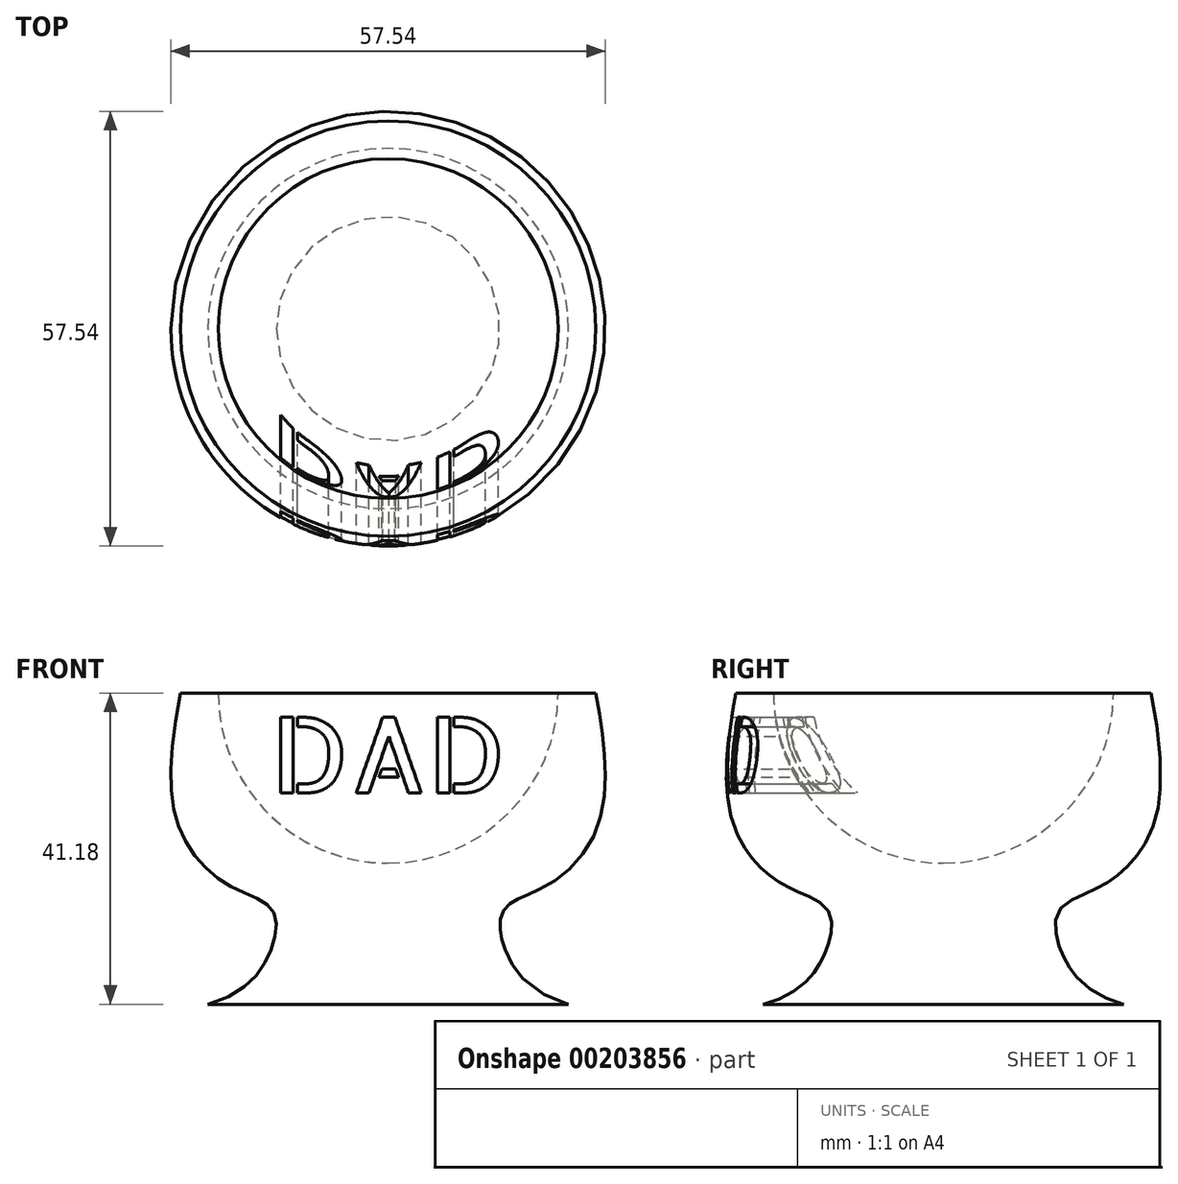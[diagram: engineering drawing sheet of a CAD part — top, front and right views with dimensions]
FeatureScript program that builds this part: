
annotation { "Feature Type Name" : "Feature", "Feature Type Description" : "" }
export const myFeature = defineFeature(function(context is Context, id is Id, definition is map)
    precondition{}
    {
        {
            var Q0;
            Q0=qCreatedBy(makeId("Front.planeOp"),FACE);
            var sketch = newSketch(context, id + "F0", { "sketchPlane" : qUnion([Q0])});
            skLineSegment(sketch, "E0", {"start": v(0, 0) * mm, "end": v(0, 41.18) * mm});
            skLineSegment(sketch, "E1", {"start": v(0, 0) * mm, "end": v(-23.86, 0) * mm});
            skCircle(sketch, "E2", {"center": v(0, 41.18) * mm, "radius": 22.5 * mm});
            skFitSpline(sketch, "E3", {"points": [v(-27.5, 41.18) * mm, v(-27.5, 22.94) * mm, v(-20.94, 15.67) * mm, v(-15.35, 12.49) * mm, v(-15.6, 6.98) * mm, v(-23.86, 0) * mm], "startDerivative": vector(-16.83, -89.57) * mm, "endDerivative": vector(-70.58, -19.3) * mm});
            skLineSegment(sketch, "E4", {"start": v(-22.5, 41.18) * mm, "end": v(-27.5, 41.18) * mm});
            skSolve(sketch);
        }
        {
            var Q0;
            {var subQ4=sQuery(id+"F0.wireOp",EDGE,"E1");Q0=makeQuery(id+"F0.imprint","IMPRINT",FACE,{"disambiguationData":[TD([[makeQuery(id+"F0.imprint","IMPRINT",EDGE,{"derivedFrom":subQ4}),-1.0]])]});}
            var Q1;
            Q1 = qSketchRegion(id + "F2", true);
            var Q2;
            Q2=sQuery(id+"F0.wireOp",EDGE,"E0");
            revolve(context, id + "F1", {"entities" : qUnion([Q0, Q1]), "axis" : qUnion([Q2]), "revolveType" : RevolveType.FULL});
        }
        {
            var Q0;
            Q0=qCreatedBy(makeId("Front.planeOp"),FACE);
            var sketch = newSketch(context, id + "F2", { "sketchPlane" : qUnion([Q0])});
            skText(sketch, "E5", { "text": "DAD", "fontName": "AllertaStencil-Regular.ttf"});
            skLineSegment(sketch, "E6", {"start": v(0, 28) * mm, "end": v(0, 0) * mm});
            const initialGuessF2  = {"E5": [-0.01552, 0.028, 1, 0, 0.01]};
            skSetInitialGuess(sketch, initialGuessF2);
            skSolve(sketch);
        }
        {
            var Q0;
            Q0 = qSketchRegion(id + "F2", true);
            extrude(context, id + "F3", {"entities" : qUnion([Q0]), "operationType" : NewBodyOperationType.REMOVE, "depth" : 57.1 * mm});
        }
    });
